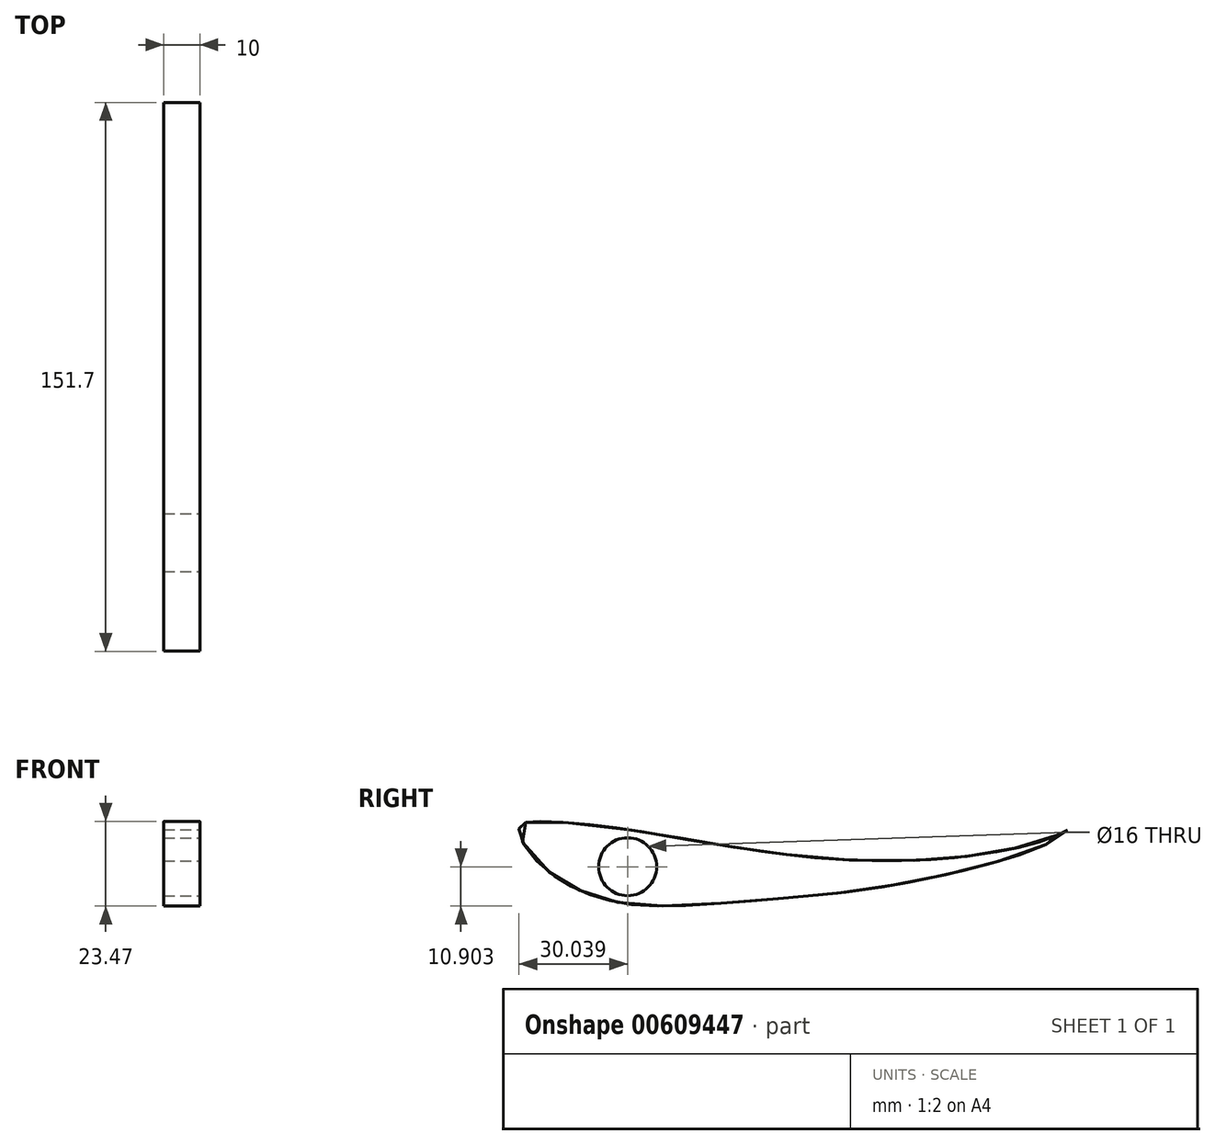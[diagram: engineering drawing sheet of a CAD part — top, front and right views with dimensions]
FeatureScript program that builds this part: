
annotation { "Feature Type Name" : "Feature", "Feature Type Description" : "" }
export const myFeature = defineFeature(function(context is Context, id is Id, definition is map)
    precondition{}
    {
        {
            var Q0;
            Q0=qCreatedBy(makeId("Right.planeOp"),FACE);
            var sketch = newSketch(context, id + "F0", { "sketchPlane" : qUnion([Q0])});
            skFitSpline(sketch, "E0", {"points": [v(-63.55, 13.08) * mm, v(-64.22, 12.9) * mm, v(-64.72, 12.57) * mm, v(-65.19, 12.02) * mm, v(-65.38, 11.07) * mm, v(-65.08, 9.35) * mm, v(-64.24, 7.3) * mm, v(-63.14, 5.55) * mm, v(-60.6, 2.51) * mm, v(-57.3, -0.37) * mm, v(-54.89, -2.16) * mm, v(-52.91, -3.45) * mm, v(-50.1, -4.96) * mm, v(-47.58, -6.13) * mm, v(-44.4, -7.34) * mm, v(-41.6, -8.18) * mm, v(-37.82, -9.07) * mm, v(-34.56, -9.54) * mm, v(-29.85, -9.95) * mm, v(-24.74, -10.06) * mm, v(-18.97, -9.86) * mm, v(-9.74, -9.3) * mm, v(-3.43, -8.78) * mm, v(4.58, -8.14) * mm, v(11.3, -7.57) * mm, v(20.6, -6.65) * mm, v(25.23, -6.13) * mm, v(34.37, -4.85) * mm, v(39.18, -4.04) * mm, v(45.28, -2.92) * mm, v(51.3, -1.61) * mm, v(56.13, -0.57) * mm, v(62.98, 1.16) * mm, v(68.85, 2.82) * mm, v(73.79, 4.39) * mm, v(79.79, 6.69) * mm, v(83.49, 8.73) * mm, v(86.32, 11.03) * mm, v(85.95, 10.8) * mm, v(83.24, 9.43) * mm, v(79.8, 8.11) * mm, v(76.9, 7.19) * mm, v(71.38, 5.87) * mm, v(66.64, 4.98) * mm, v(62.07, 4.24) * mm, v(56.48, 3.52) * mm, v(53.13, 3.2) * mm, v(44.93, 2.64) * mm, v(36.43, 2.47) * mm, v(26.9, 2.64) * mm, v(18.6, 3.15) * mm, v(9.98, 4.06) * mm, v(2.95, 4.95) * mm, v(-2.09, 5.68) * mm, v(-8.9, 6.76) * mm, v(-14.61, 7.68) * mm, v(-23.14, 9.08) * mm, v(-29.66, 10.16) * mm, v(-32, 10.57) * mm, v(-38.86, 11.6) * mm, v(-46.16, 12.48) * mm, v(-53.82, 13.1) * mm, v(-59, 13.4) * mm, v(-62.52, 13.22) * mm, v(-63.55, 13.08) * mm]});
            skPoint(sketch, "E1", {"position": v(-35.34, 0.83) * mm});
            skCircle(sketch, "E2", {"center": v(-35.34, 0.83) * mm, "radius": 8 * mm});
            skSolve(sketch);
        }
        {
            var Q0;
            Q0=makeQuery(id+"F0.imprint","IMPRINT",FACE,{"disambiguationData":[TD([[makeQuery(id+"F0.imprint","IMPRINT",EDGE,{"derivedFrom":sQuery(id+"F0.wireOp",EDGE,"E0")}),1.0]])]});
            extrude(context, id + "F1", {"entities" : qUnion([Q0]), "oppositeDirection" : true, "depth" : 10 * mm, "offsetDistance" : 25.4 * mm});
        }
    });
